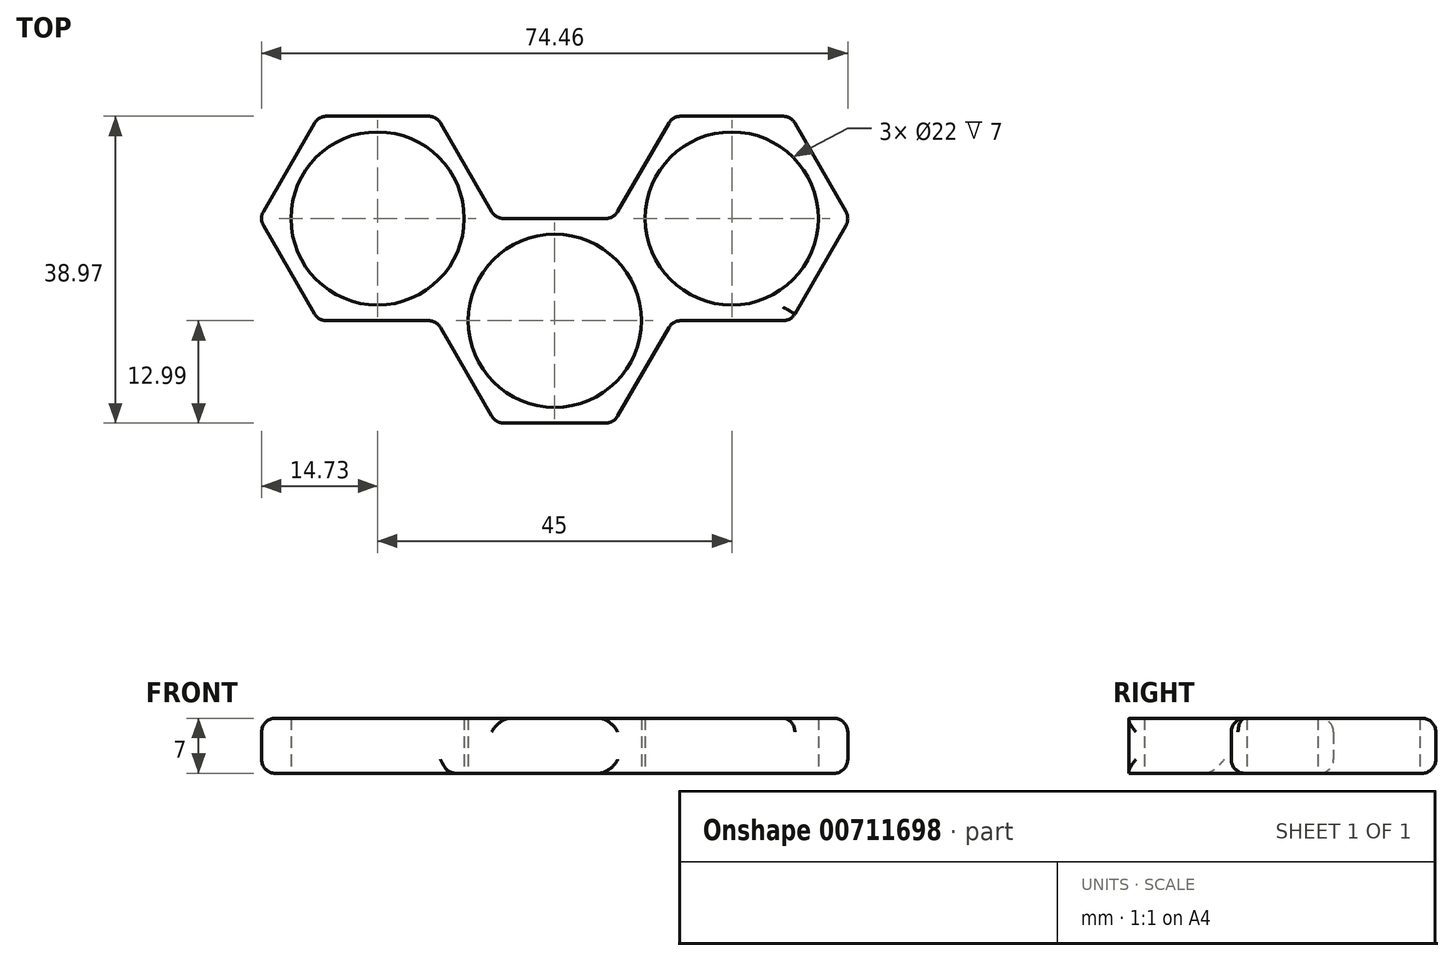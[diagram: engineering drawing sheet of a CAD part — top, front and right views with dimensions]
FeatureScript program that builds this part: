
annotation { "Feature Type Name" : "Feature", "Feature Type Description" : "" }
export const myFeature = defineFeature(function(context is Context, id is Id, definition is map)
    precondition{}
    {
        {
            var Q0;
            Q0=qCreatedBy(makeId("Top.planeOp"),FACE);
            var sketch = newSketch(context, id + "F0", { "sketchPlane" : qUnion([Q0])});
            skCircle(sketch, "E0.cCircle", {"center": v(0, 0) * mm, "radius": 13 * mm, "construction": true});
            skLineSegment(sketch, "E0.0", {"start": v(7.5, -13) * mm, "end": v(-7.5, -13) * mm});
            skLineSegment(sketch, "E0.1", {"start": v(-7.5, -13) * mm, "end": v(-15, 0) * mm});
            skLineSegment(sketch, "E0.2", {"start": v(-15, 0) * mm, "end": v(-7.5, 13) * mm});
            skLineSegment(sketch, "E0.3", {"start": v(-7.5, 13) * mm, "end": v(7.5, 13) * mm});
            skLineSegment(sketch, "E0.4", {"start": v(7.5, 13) * mm, "end": v(15, 0) * mm});
            skLineSegment(sketch, "E0.5", {"start": v(15, 0) * mm, "end": v(7.5, -13) * mm});
            skPoint(sketch, "E0.0.midPoint", {"position": v(0, -13) * mm});
            skCircle(sketch, "E1.cCircle", {"center": v(0, -25.98) * mm, "radius": 13 * mm, "construction": true});
            skLineSegment(sketch, "E1.0", {"start": v(-7.5, -13) * mm, "end": v(7.5, -13) * mm});
            skLineSegment(sketch, "E1.1", {"start": v(7.5, -13) * mm, "end": v(15, -25.98) * mm});
            skLineSegment(sketch, "E1.2", {"start": v(15, -25.98) * mm, "end": v(7.5, -38.97) * mm});
            skLineSegment(sketch, "E1.3", {"start": v(7.5, -38.97) * mm, "end": v(-7.5, -38.97) * mm});
            skLineSegment(sketch, "E1.4", {"start": v(-7.5, -38.97) * mm, "end": v(-15, -25.98) * mm});
            skLineSegment(sketch, "E1.5", {"start": v(-15, -25.98) * mm, "end": v(-7.5, -13) * mm});
            skCircle(sketch, "E2.cCircle", {"center": v(22.5, 13) * mm, "radius": 13 * mm, "construction": true});
            skLineSegment(sketch, "E2.0", {"start": v(30, 0) * mm, "end": v(15, 0) * mm});
            skLineSegment(sketch, "E2.1", {"start": v(15, 0) * mm, "end": v(7.5, 13) * mm});
            skLineSegment(sketch, "E2.2", {"start": v(7.5, 13) * mm, "end": v(15, 25.98) * mm});
            skLineSegment(sketch, "E2.3", {"start": v(15, 25.98) * mm, "end": v(30, 25.98) * mm});
            skLineSegment(sketch, "E2.4", {"start": v(30, 25.98) * mm, "end": v(37.5, 13) * mm});
            skLineSegment(sketch, "E2.5", {"start": v(37.5, 13) * mm, "end": v(30, 0) * mm});
            skPoint(sketch, "E2.0.midPoint", {"position": v(22.5, 0) * mm});
            skCircle(sketch, "E3.cCircle", {"center": v(-22.5, 13) * mm, "radius": 13 * mm, "construction": true});
            skLineSegment(sketch, "E3.0", {"start": v(-15, 0) * mm, "end": v(-30, 0) * mm});
            skLineSegment(sketch, "E3.1", {"start": v(-30, 0) * mm, "end": v(-37.5, 13) * mm});
            skLineSegment(sketch, "E3.2", {"start": v(-37.5, 13) * mm, "end": v(-30, 25.98) * mm});
            skLineSegment(sketch, "E3.3", {"start": v(-30, 25.98) * mm, "end": v(-15, 25.98) * mm});
            skLineSegment(sketch, "E3.4", {"start": v(-15, 25.98) * mm, "end": v(-7.5, 13) * mm});
            skLineSegment(sketch, "E3.5", {"start": v(-7.5, 13) * mm, "end": v(-15, 0) * mm});
            skPoint(sketch, "E3.0.midPoint", {"position": v(-22.5, 0) * mm});
            skCircle(sketch, "E4", {"center": v(22.5, 13) * mm, "radius": 11 * mm});
            skCircle(sketch, "E5", {"center": v(0, 0) * mm, "radius": 11 * mm});
            skCircle(sketch, "E6", {"center": v(-22.5, 13) * mm, "radius": 11 * mm});
            skCircle(sketch, "E7", {"center": v(0, -25.98) * mm, "radius": 11 * mm});
            skSolve(sketch);
        }
        {
            var Q0;
            Q0=makeQuery(id+"F0.imprint","IMPRINT",FACE,{"disambiguationData":[TD([[makeQuery(id+"F0.imprint","IMPRINT",EDGE,{"derivedFrom":sQuery(id+"F0.wireOp",EDGE,"E0.1")}),-1.0]])]});
            var Q1;
            Q1=makeQuery(id+"F0.imprint","IMPRINT",FACE,{"disambiguationData":[TD([[makeQuery(id+"F0.imprint","IMPRINT",EDGE,{"derivedFrom":sQuery(id+"F0.wireOp",EDGE,"E2.0")}),-1.0]])]});
            var Q2;
            Q2=makeQuery(id+"F0.imprint","IMPRINT",FACE,{"disambiguationData":[TD([[makeQuery(id+"F0.imprint","IMPRINT",EDGE,{"derivedFrom":sQuery(id+"F0.wireOp",EDGE,"E1.0")}),-1.0]])]});
            var Q3;
            Q3=makeQuery(id+"F0.imprint","IMPRINT",FACE,{"disambiguationData":[TD([[makeQuery(id+"F0.imprint","IMPRINT",EDGE,{"derivedFrom":sQuery(id+"F0.wireOp",EDGE,"E3.0")}),-1.0]])]});
            extrude(context, id + "F1", {"entities" : qUnion([Q0, Q1, Q2, Q3]), "depth" : 7 * mm, "offsetDistance" : 25 * mm});
        }
        {
            var Q0;
            Q0=makeQuery(id+"F1.opExtrude","SWEPT_EDGE",EDGE,{"disambiguationData":[OSD([sQuery(id+"F0.wireOp",EDGE,"E1.2"),sQuery(id+"F0.wireOp",EDGE,"E1.3")])]});
            var Q1;
            Q1=makeQuery(id+"F1.opExtrude","SWEPT_EDGE",EDGE,{"disambiguationData":[OSD([sQuery(id+"F0.wireOp",EDGE,"E1.1"),sQuery(id+"F0.wireOp",EDGE,"E1.2")])]});
            var Q2;
            Q2=makeQuery(id+"F1.opExtrude","CAP_EDGE",EDGE,{"disambiguationData":[OSD([sQuery(id+"F0.wireOp",EDGE,"E1.2")])],"isStart":true});
            var Q3;
            Q3=makeQuery(id+"F1.opExtrude","CAP_EDGE",EDGE,{"disambiguationData":[OSD([sQuery(id+"F0.wireOp",EDGE,"E1.2")])],"isStart":false});
            var Q4;
            Q4=makeQuery(id+"F1.opExtrude","CAP_EDGE",EDGE,{"disambiguationData":[OSD([sQuery(id+"F0.wireOp",EDGE,"E1.3")])],"isStart":false});
            var Q5;
            Q5=makeQuery(id+"F1.opExtrude","CAP_EDGE",EDGE,{"disambiguationData":[OSD([sQuery(id+"F0.wireOp",EDGE,"E1.1")])],"isStart":false});
            var Q6;
            Q6=makeQuery(id+"F1.opExtrude","CAP_EDGE",EDGE,{"disambiguationData":[OSD([sQuery(id+"F0.wireOp",EDGE,"E1.1")])],"isStart":true});
            var Q7;
            Q7=makeQuery(id+"F1.opExtrude","CAP_EDGE",EDGE,{"disambiguationData":[OSD([sQuery(id+"F0.wireOp",EDGE,"E0.5")])],"isStart":true});
            var Q8;
            Q8=makeQuery(id+"F1.opExtrude","SWEPT_EDGE",EDGE,{"disambiguationData":[OSD([sQuery(id+"F0.wireOp",EDGE,"E0.5"),sQuery(id+"F0.wireOp",EDGE,"E1.0"),sQuery(id+"F0.wireOp",EDGE,"E1.1")])]});
            var Q9;
            Q9=makeQuery(id+"F1.opExtrude","CAP_EDGE",EDGE,{"disambiguationData":[OSD([sQuery(id+"F0.wireOp",EDGE,"E0.5")])],"isStart":false});
            var Q10;
            Q10=makeQuery(id+"F1.opExtrude","SWEPT_EDGE",EDGE,{"disambiguationData":[OSD([sQuery(id+"F0.wireOp",EDGE,"E0.5"),sQuery(id+"F0.wireOp",EDGE,"E2.0"),sQuery(id+"F0.wireOp",EDGE,"E2.1")])]});
            var Q11;
            Q11=makeQuery(id+"F1.opExtrude","CAP_EDGE",EDGE,{"disambiguationData":[OSD([sQuery(id+"F0.wireOp",EDGE,"E2.0")])],"isStart":true});
            var Q12;
            Q12=makeQuery(id+"F1.opExtrude","CAP_EDGE",EDGE,{"disambiguationData":[OSD([sQuery(id+"F0.wireOp",EDGE,"E2.0")])],"isStart":false});
            var Q13;
            Q13=makeQuery(id+"F1.opExtrude","SWEPT_EDGE",EDGE,{"disambiguationData":[OSD([sQuery(id+"F0.wireOp",EDGE,"E2.0"),sQuery(id+"F0.wireOp",EDGE,"E2.5")])]});
            var Q14;
            Q14=makeQuery(id+"F1.opExtrude","CAP_EDGE",EDGE,{"disambiguationData":[OSD([sQuery(id+"F0.wireOp",EDGE,"E2.5")])],"isStart":true});
            var Q15;
            Q15=makeQuery(id+"F1.opExtrude","CAP_EDGE",EDGE,{"disambiguationData":[OSD([sQuery(id+"F0.wireOp",EDGE,"E2.5")])],"isStart":false});
            var Q16;
            Q16=makeQuery(id+"F1.opExtrude","CAP_EDGE",EDGE,{"disambiguationData":[OSD([sQuery(id+"F0.wireOp",EDGE,"E2.4")])],"isStart":true});
            var Q17;
            Q17=makeQuery(id+"F1.opExtrude","CAP_EDGE",EDGE,{"disambiguationData":[OSD([sQuery(id+"F0.wireOp",EDGE,"E2.4")])],"isStart":false});
            var Q18;
            Q18=makeQuery(id+"F1.opExtrude","SWEPT_EDGE",EDGE,{"disambiguationData":[OSD([sQuery(id+"F0.wireOp",EDGE,"E2.4"),sQuery(id+"F0.wireOp",EDGE,"E2.5")])]});
            var Q19;
            Q19=makeQuery(id+"F1.opExtrude","SWEPT_EDGE",EDGE,{"disambiguationData":[OSD([sQuery(id+"F0.wireOp",EDGE,"E2.3"),sQuery(id+"F0.wireOp",EDGE,"E2.4")])]});
            var Q20;
            Q20=makeQuery(id+"F1.opExtrude","CAP_EDGE",EDGE,{"disambiguationData":[OSD([sQuery(id+"F0.wireOp",EDGE,"E2.3")])],"isStart":false});
            var Q21;
            Q21=makeQuery(id+"F1.opExtrude","CAP_EDGE",EDGE,{"disambiguationData":[OSD([sQuery(id+"F0.wireOp",EDGE,"E2.3")])],"isStart":true});
            var Q22;
            Q22=makeQuery(id+"F1.opExtrude","CAP_EDGE",EDGE,{"disambiguationData":[OSD([sQuery(id+"F0.wireOp",EDGE,"E2.2")])],"isStart":false});
            var Q23;
            Q23=makeQuery(id+"F1.opExtrude","CAP_EDGE",EDGE,{"disambiguationData":[OSD([sQuery(id+"F0.wireOp",EDGE,"E2.2")])],"isStart":true});
            var Q24;
            Q24=makeQuery(id+"F1.opExtrude","CAP_EDGE",EDGE,{"disambiguationData":[OSD([sQuery(id+"F0.wireOp",EDGE,"E0.3")])],"isStart":false});
            var Q25;
            Q25=makeQuery(id+"F1.opExtrude","CAP_EDGE",EDGE,{"disambiguationData":[OSD([sQuery(id+"F0.wireOp",EDGE,"E0.3")])],"isStart":true});
            var Q26;
            Q26=makeQuery(id+"F1.opExtrude","CAP_EDGE",EDGE,{"disambiguationData":[OSD([sQuery(id+"F0.wireOp",EDGE,"E3.4")])],"isStart":false});
            var Q27;
            Q27=makeQuery(id+"F1.opExtrude","CAP_EDGE",EDGE,{"disambiguationData":[OSD([sQuery(id+"F0.wireOp",EDGE,"E3.4")])],"isStart":true});
            var Q28;
            Q28=makeQuery(id+"F1.opExtrude","CAP_EDGE",EDGE,{"disambiguationData":[OSD([sQuery(id+"F0.wireOp",EDGE,"E3.3")])],"isStart":true});
            var Q29;
            Q29=makeQuery(id+"F1.opExtrude","SWEPT_EDGE",EDGE,{"disambiguationData":[OSD([sQuery(id+"F0.wireOp",EDGE,"E3.3"),sQuery(id+"F0.wireOp",EDGE,"E3.4")])]});
            var Q30;
            Q30=makeQuery(id+"F1.opExtrude","CAP_EDGE",EDGE,{"disambiguationData":[OSD([sQuery(id+"F0.wireOp",EDGE,"E3.3")])],"isStart":false});
            var Q31;
            Q31=makeQuery(id+"F1.opExtrude","SWEPT_EDGE",EDGE,{"disambiguationData":[OSD([sQuery(id+"F0.wireOp",EDGE,"E3.2"),sQuery(id+"F0.wireOp",EDGE,"E3.3")])]});
            var Q32;
            Q32=makeQuery(id+"F1.opExtrude","CAP_EDGE",EDGE,{"disambiguationData":[OSD([sQuery(id+"F0.wireOp",EDGE,"E3.2")])],"isStart":false});
            var Q33;
            Q33=makeQuery(id+"F1.opExtrude","CAP_EDGE",EDGE,{"disambiguationData":[OSD([sQuery(id+"F0.wireOp",EDGE,"E3.2")])],"isStart":true});
            var Q34;
            Q34=makeQuery(id+"F1.opExtrude","SWEPT_EDGE",EDGE,{"disambiguationData":[OSD([sQuery(id+"F0.wireOp",EDGE,"E3.1"),sQuery(id+"F0.wireOp",EDGE,"E3.2")])]});
            var Q35;
            Q35=makeQuery(id+"F1.opExtrude","CAP_EDGE",EDGE,{"disambiguationData":[OSD([sQuery(id+"F0.wireOp",EDGE,"E3.1")])],"isStart":false});
            var Q36;
            Q36=makeQuery(id+"F1.opExtrude","CAP_EDGE",EDGE,{"disambiguationData":[OSD([sQuery(id+"F0.wireOp",EDGE,"E3.1")])],"isStart":true});
            var Q37;
            Q37=makeQuery(id+"F1.opExtrude","CAP_EDGE",EDGE,{"disambiguationData":[OSD([sQuery(id+"F0.wireOp",EDGE,"E3.0")])],"isStart":true});
            var Q38;
            Q38=makeQuery(id+"F1.opExtrude","SWEPT_EDGE",EDGE,{"disambiguationData":[OSD([sQuery(id+"F0.wireOp",EDGE,"E3.0"),sQuery(id+"F0.wireOp",EDGE,"E3.1")])]});
            var Q39;
            Q39=makeQuery(id+"F1.opExtrude","CAP_EDGE",EDGE,{"disambiguationData":[OSD([sQuery(id+"F0.wireOp",EDGE,"E3.0")])],"isStart":false});
            var Q40;
            Q40=makeQuery(id+"F1.opExtrude","SWEPT_EDGE",EDGE,{"disambiguationData":[OSD([sQuery(id+"F0.wireOp",EDGE,"E0.1"),sQuery(id+"F0.wireOp",EDGE,"E3.0"),sQuery(id+"F0.wireOp",EDGE,"E3.5")])]});
            var Q41;
            Q41=makeQuery(id+"F1.opExtrude","CAP_EDGE",EDGE,{"disambiguationData":[OSD([sQuery(id+"F0.wireOp",EDGE,"E0.1")])],"isStart":false});
            var Q42;
            Q42=makeQuery(id+"F1.opExtrude","SWEPT_EDGE",EDGE,{"disambiguationData":[OSD([sQuery(id+"F0.wireOp",EDGE,"E0.1"),sQuery(id+"F0.wireOp",EDGE,"E1.0"),sQuery(id+"F0.wireOp",EDGE,"E1.5")])]});
            var Q43;
            Q43=makeQuery(id+"F1.opExtrude","CAP_EDGE",EDGE,{"disambiguationData":[OSD([sQuery(id+"F0.wireOp",EDGE,"E1.5")])],"isStart":true});
            var Q44;
            Q44=makeQuery(id+"F1.opExtrude","CAP_EDGE",EDGE,{"disambiguationData":[OSD([sQuery(id+"F0.wireOp",EDGE,"E1.5")])],"isStart":false});
            var Q45;
            Q45=makeQuery(id+"F1.opExtrude","SWEPT_EDGE",EDGE,{"disambiguationData":[OSD([sQuery(id+"F0.wireOp",EDGE,"E1.4"),sQuery(id+"F0.wireOp",EDGE,"E1.5")])]});
            var Q46;
            Q46=makeQuery(id+"F1.opExtrude","CAP_EDGE",EDGE,{"disambiguationData":[OSD([sQuery(id+"F0.wireOp",EDGE,"E1.4")])],"isStart":false});
            var Q47;
            Q47=makeQuery(id+"F1.opExtrude","CAP_EDGE",EDGE,{"disambiguationData":[OSD([sQuery(id+"F0.wireOp",EDGE,"E1.4")])],"isStart":true});
            var Q48;
            Q48=makeQuery(id+"F1.opExtrude","SWEPT_EDGE",EDGE,{"disambiguationData":[OSD([sQuery(id+"F0.wireOp",EDGE,"E1.3"),sQuery(id+"F0.wireOp",EDGE,"E1.4")])]});
            var Q49;
            Q49=makeQuery(id+"F1.opExtrude","CAP_EDGE",EDGE,{"disambiguationData":[OSD([sQuery(id+"F0.wireOp",EDGE,"E1.3")])],"isStart":true});
            var Q50;
            Q50=makeQuery(id+"F1.opExtrude","SWEPT_EDGE",EDGE,{"disambiguationData":[OSD([sQuery(id+"F0.wireOp",EDGE,"E0.3"),sQuery(id+"F0.wireOp",EDGE,"E3.4"),sQuery(id+"F0.wireOp",EDGE,"E3.5")])]});
            var Q51;
            Q51=makeQuery(id+"F1.opExtrude","SWEPT_EDGE",EDGE,{"disambiguationData":[OSD([sQuery(id+"F0.wireOp",EDGE,"E0.3"),sQuery(id+"F0.wireOp",EDGE,"E2.1"),sQuery(id+"F0.wireOp",EDGE,"E2.2")])]});
            var Q52;
            Q52=makeQuery(id+"F1.opExtrude","SWEPT_EDGE",EDGE,{"disambiguationData":[OSD([sQuery(id+"F0.wireOp",EDGE,"E2.2"),sQuery(id+"F0.wireOp",EDGE,"E2.3")])]});
            fillet(context, id + "F2", {"entities" : qUnion([Q0, Q1, Q2, Q3, Q4, Q5, Q6, Q7, Q8, Q9, Q10, Q11, Q12, Q13, Q14, Q15, Q16, Q17, Q18, Q19, Q20, Q21, Q22, Q23, Q24, Q25, Q26, Q27, Q28, Q29, Q30, Q31, Q32, Q33, Q34, Q35, Q36, Q37, Q38, Q39, Q40, Q41, Q42, Q43, Q44, Q45, Q46, Q47, Q48, Q49, Q50, Q51, Q52]), "radius" : 1.75 * mm, "tangentPropagation" : true, "allowEdgeOverflow" : false});
        }
    });
